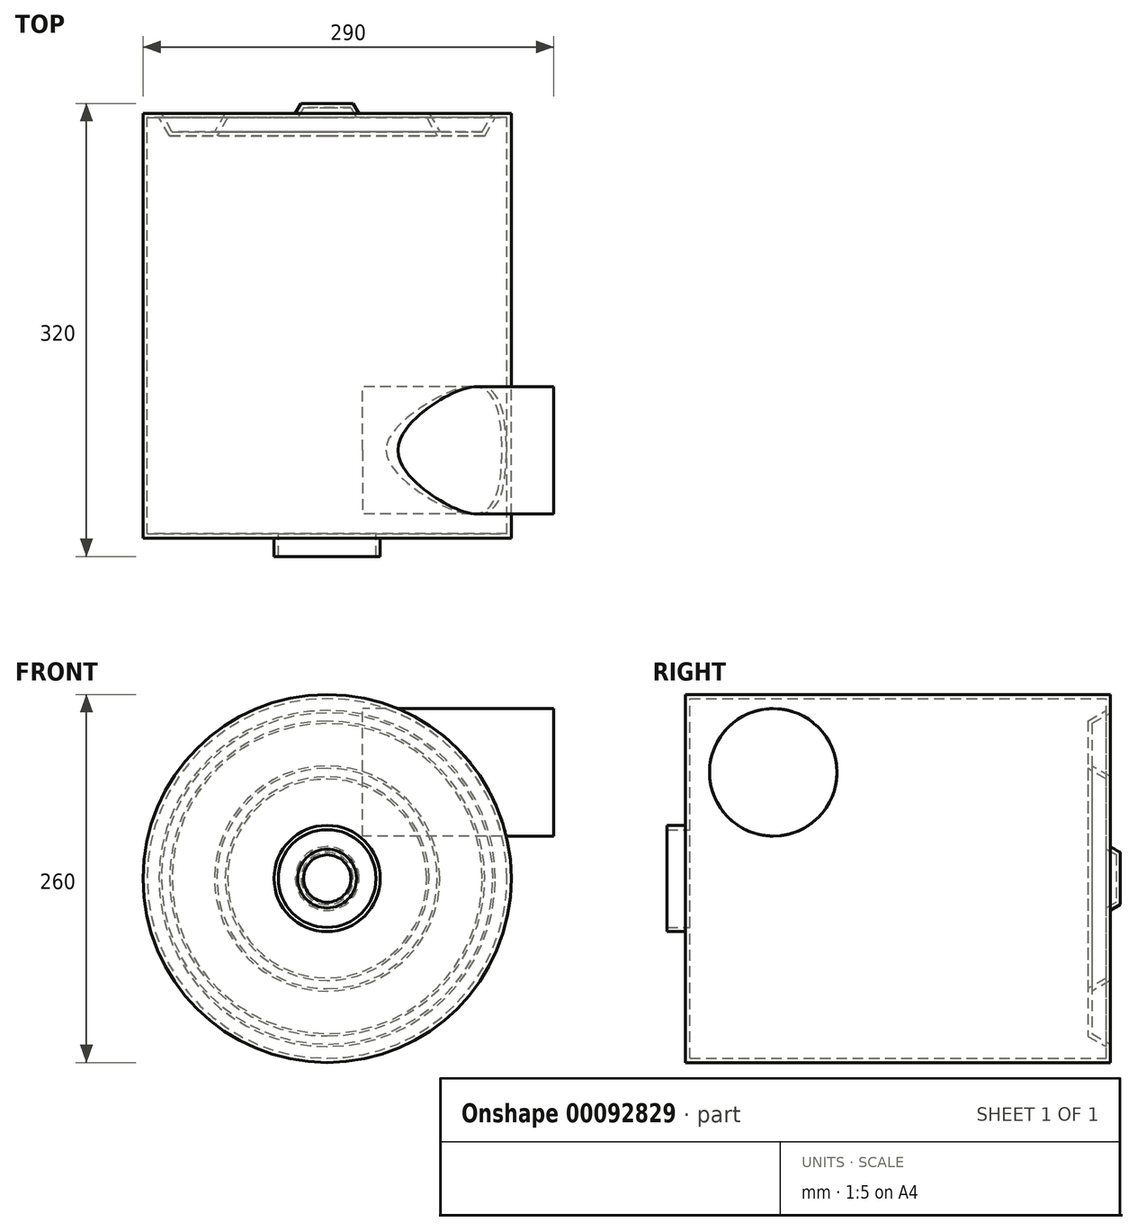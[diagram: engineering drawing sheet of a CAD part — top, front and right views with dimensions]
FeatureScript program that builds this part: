
annotation { "Feature Type Name" : "Feature", "Feature Type Description" : "" }
export const myFeature = defineFeature(function(context is Context, id is Id, definition is map)
    precondition{}
    {
        {
            var Q0;
            Q0=qCreatedBy(makeId("Front.planeOp"),FACE);
            var sketch = newSketch(context, id + "F0", { "sketchPlane" : qUnion([Q0])});
            skCircle(sketch, "E0", {"center": v(0, 0) * mm, "radius": 130 * mm});
            skSolve(sketch);
        }
        {
            var Q0;
            Q0=makeQuery(id+"F0.imprint","IMPRINT",FACE,{"disambiguationData":[TD([[makeQuery(id+"F0.imprint","IMPRINT",EDGE,{"derivedFrom":sQuery(id+"F0.wireOp",EDGE,"E0")}),1.0]])]});
            extrude(context, id + "F1", {"entities" : qUnion([Q0]), "depth" : 300 * mm});
        }
        {
            var Q0;
            Q0=makeQuery(id+"F1.opExtrude","CAP_FACE",FACE,{"disambiguationData":[OSD([sQuery(id+"F0.wireOp",EDGE,"E0")])],"isStart":false});
            var sketch = newSketch(context, id + "F2", { "sketchPlane" : qUnion([Q0])});
            skCircle(sketch, "E1", {"center": v(0, 0) * mm, "radius": 37.5 * mm});
            skSolve(sketch);
        }
        {
            var Q0;
            Q0=makeQuery(id+"F2.imprint","IMPRINT",FACE,{"disambiguationData":[TD([[makeQuery(id+"F2.imprint","IMPRINT",EDGE,{"derivedFrom":sQuery(id+"F2.wireOp",EDGE,"E1")}),1.0]])]});
            extrude(context, id + "F3", {"entities" : qUnion([Q0]), "operationType" : NewBodyOperationType.ADD, "depth" : 13 * mm});
        }
        {
            var Q0;
            Q0=makeQuery(id+"F1.opExtrude","CAP_FACE",FACE,{"disambiguationData":[OSD([sQuery(id+"F0.wireOp",EDGE,"E0")])],"isStart":true});
            var sketch = newSketch(context, id + "F4", { "sketchPlane" : qUnion([Q0])});
            skCircle(sketch, "E2", {"center": v(0, 0) * mm, "radius": 117 * mm});
            skCircle(sketch, "E3", {"center": v(0, 0) * mm, "radius": 72 * mm});
            skSolve(sketch);
        }
        {
            var Q0;
            Q0=makeQuery(id+"F4.imprint","IMPRINT",FACE,{"disambiguationData":[TD([[makeQuery(id+"F4.imprint","IMPRINT",EDGE,{"derivedFrom":sQuery(id+"F4.wireOp",EDGE,"E2")}),1.0]])]});
            extrude(context, id + "F5", {"entities" : qUnion([Q0]), "operationType" : NewBodyOperationType.REMOVE, "oppositeDirection" : true, "depth" : 13 * mm, "hasDraft" : true, "draftAngle" : 30 * degree, "draftPullDirection" : true});
        }
        {
            var Q0;
            Q0=makeQuery(id+"F4.imprint","IMPRINT",FACE,{"disambiguationData":[TD([[makeQuery(id+"F4.imprint","IMPRINT",EDGE,{"derivedFrom":sQuery(id+"F4.wireOp",EDGE,"E3")}),1.0]])]});
            var sketch = newSketch(context, id + "F6", { "sketchPlane" : qUnion([Q0])});
            skCircle(sketch, "E4", {"center": v(0, 0) * mm, "radius": 22.5 * mm});
            skSolve(sketch);
        }
        {
            var Q0;
            Q0=makeQuery(id+"F6.imprint","IMPRINT",FACE,{"disambiguationData":[TD([[makeQuery(id+"F6.imprint","IMPRINT",EDGE,{"derivedFrom":sQuery(id+"F6.wireOp",EDGE,"E4")}),1.0]])]});
            extrude(context, id + "F7", {"entities" : qUnion([Q0]), "operationType" : NewBodyOperationType.ADD, "depth" : 7 * mm, "hasDraft" : true, "draftAngle" : 30 * degree, "draftPullDirection" : true});
        }
        {
            var Q0;
            Q0=makeQuery(id+"F3.opExtrude","CAP_FACE",FACE,{"disambiguationData":[OSD([sQuery(id+"F2.wireOp",EDGE,"E1")])],"isStart":false});
            shell(context, id + "F8", {"entities" : qUnion([Q0]), "thickness" : 3 * mm});
        }
        {
            var Q0;
            Q0=qCreatedBy(makeId("Right.planeOp"),FACE);
            var sketch = newSketch(context, id + "F9", { "sketchPlane" : qUnion([Q0])});
            skCircle(sketch, "E5", {"center": v(-238, 75) * mm, "radius": 45 * mm});
            skSolve(sketch);
        }
        {
            var Q0;
            Q0 = qSketchRegion(id + "F9", true);
            extrude(context, id + "F10", {"entities" : qUnion([Q0]), "operationType" : NewBodyOperationType.ADD, "depth" : 160 * mm, "hasSecondDirection" : true, "secondDirectionOppositeDirection" : false, "secondDirectionDepth" : 25 * mm});
        }
    });
